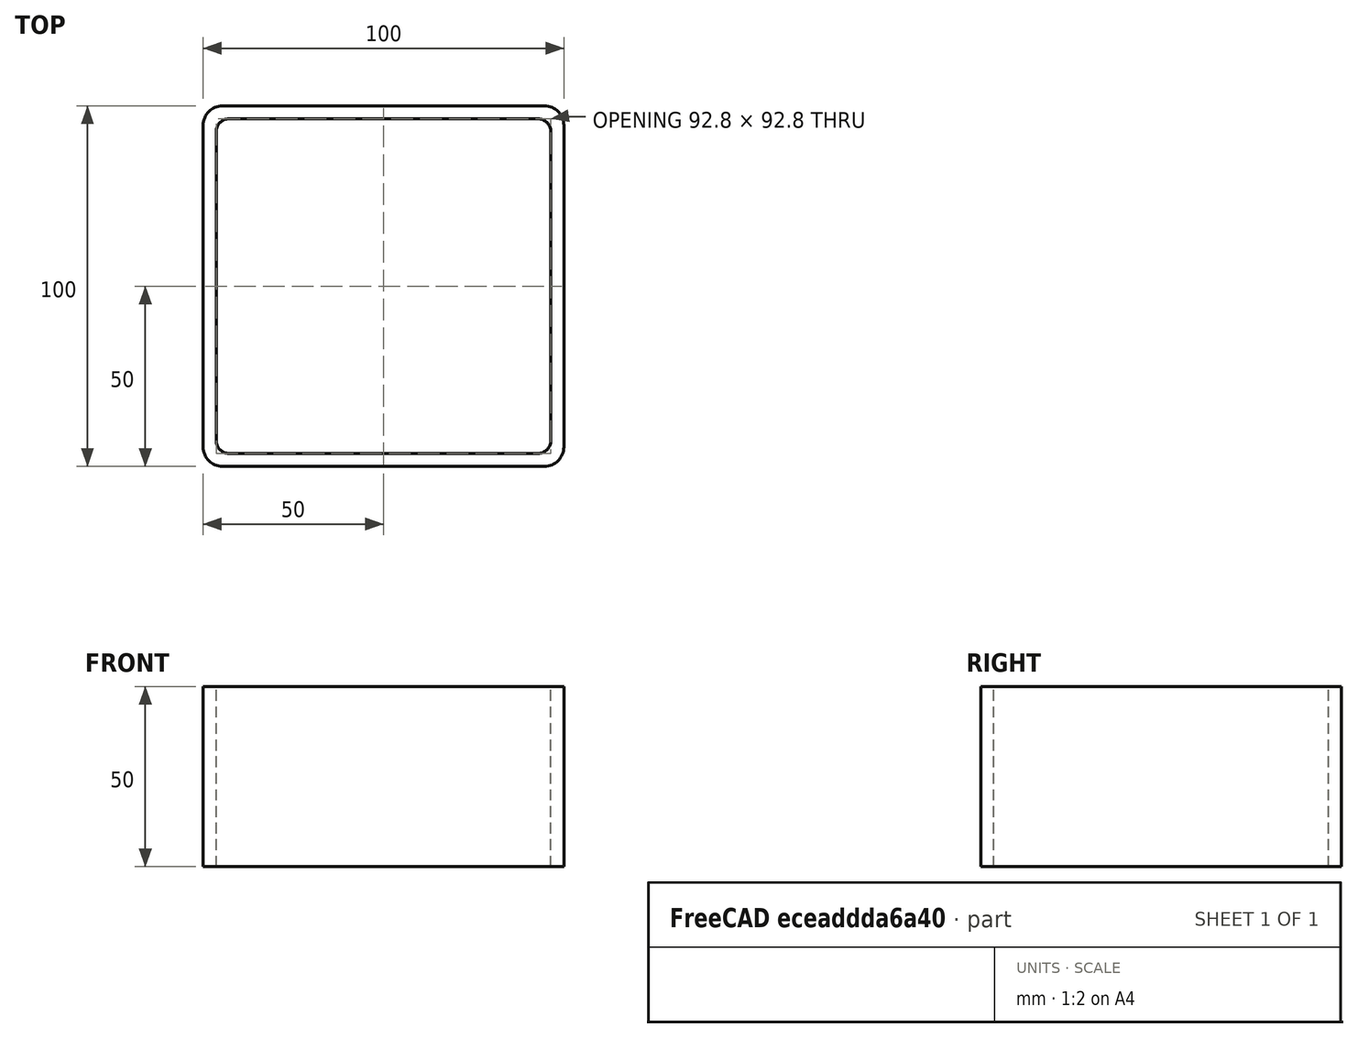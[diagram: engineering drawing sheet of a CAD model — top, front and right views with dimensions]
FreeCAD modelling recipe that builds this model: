
FCSTD DOCUMENT  (FreeCAD 0.15R4671 (Git))
Label: Square hollow section 100x100x3.6 EN10219 S235JRH
License: All rights reserved
LicenseURL: http://en.wikipedia.org/wiki/All_rights_reserved
objects: Sketcher::SketchObject×1, Part::Extrusion×1
note: 2 computed .brp shape members not serialized (recipe doc carries the construction recipe); baked Part::Feature solids carry a one-line shape summary decoded from their .brp

FEATURE [Sketcher::SketchObject] Sketch
  sketch-geometry (16):
    g0: LineSegment StartX=-42.8 StartY=46.4 StartZ=0 EndX=42.8 EndY=46.4 EndZ=0
    g1: LineSegment StartX=46.4 StartY=42.8 StartZ=0 EndX=46.4 EndY=-42.8 EndZ=0
    g2: LineSegment StartX=42.8 StartY=-46.4 StartZ=0 EndX=-42.8 EndY=-46.4 EndZ=0
    g3: LineSegment StartX=-46.4 StartY=-42.8 StartZ=0 EndX=-46.4 EndY=42.8 EndZ=0
    g4: LineSegment StartX=-44.6 StartY=50 StartZ=0 EndX=44.6 EndY=50 EndZ=0
    g5: LineSegment StartX=50 StartY=44.6 StartZ=0 EndX=50 EndY=-44.6 EndZ=0
    g6: LineSegment StartX=44.6 StartY=-50 StartZ=0 EndX=-44.6 EndY=-50 EndZ=0
    g7: LineSegment StartX=-50 StartY=-44.6 StartZ=0 EndX=-50 EndY=44.6 EndZ=0
    g8: ArcOfCircle CenterX=-42.8 CenterY=42.8 CenterZ=0 NormalX=0 NormalY=0 NormalZ=1 Radius=3.6 StartAngle=1.5708 EndAngle=3.14159
    g9: ArcOfCircle CenterX=42.8 CenterY=42.8 CenterZ=0 NormalX=0 NormalY=0 NormalZ=1 Radius=3.6 StartAngle=0 EndAngle=1.5708
    g10: ArcOfCircle CenterX=42.8 CenterY=-42.8 CenterZ=0 NormalX=0 NormalY=0 NormalZ=1 Radius=3.6 StartAngle=4.71239 EndAngle=6.28319
    g11: ArcOfCircle CenterX=-42.8 CenterY=-42.8 CenterZ=0 NormalX=0 NormalY=0 NormalZ=1 Radius=3.6 StartAngle=3.14159 EndAngle=4.71239
    g12: ArcOfCircle CenterX=44.6 CenterY=44.6 CenterZ=0 NormalX=0 NormalY=0 NormalZ=1 Radius=5.4 StartAngle=0 EndAngle=1.5708
    g13: ArcOfCircle CenterX=44.6 CenterY=-44.6 CenterZ=0 NormalX=0 NormalY=0 NormalZ=1 Radius=5.4 StartAngle=4.71239 EndAngle=6.28319
    g14: ArcOfCircle CenterX=-44.6 CenterY=-44.6 CenterZ=0 NormalX=0 NormalY=0 NormalZ=1 Radius=5.4 StartAngle=3.14159 EndAngle=4.71239
    g15: ArcOfCircle CenterX=-44.6 CenterY=44.6 CenterZ=0 NormalX=0 NormalY=0 NormalZ=1 Radius=5.4 StartAngle=1.5708 EndAngle=3.14159
  constraints (36):
    c: Horizontal(g2)
    c: Vertical(g3)
    c: Horizontal(g6)
    c: Vertical(g7)
    c: Tangent(g3,g8) = 1.5708
    c: Tangent(g0,g8) = 1.5708
    c: Tangent(g0,g9) = 1.5708
    c: Tangent(g1,g9) = 1.5708
    c: Tangent(g1,g10) = 1.5708
    c: Tangent(g2,g10) = 1.5708
    c: Tangent(g2,g11) = 1.5708
    c: Tangent(g3,g11) = 1.5708
    c: Tangent(g4,g12) = 1.5708
    c: Tangent(g5,g12) = 1.5708
    c: Tangent(g5,g13) = 1.5708
    c: Tangent(g6,g13) = 1.5708
    c: Tangent(g6,g14) = 1.5708
    c: Tangent(g7,g14) = 1.5708
    c: Tangent(g7,g15) = 1.5708
    c: Tangent(g4,g15) = 1.5708
    c: Equal(g9,g8)
    c: Equal(g9,g11)
    c: Equal(g9,g10)
    c: Equal(g12,g15)
    c: Equal(g12,g14)
    c: Equal(g12,g13)
    c: Symmetric(g4,g6,g-1)
    c: Symmetric(g7,g5,g-2)
    c: DistanceY(g4,g6) = -100
    c: DistanceX(g7,g5) = 100
    c: Symmetric(g3,g1,g-2)
    c: Symmetric(g0,g2,g-1)
    c: DistanceY(g0,g4) = 3.6
    c: DistanceX(g5,g1) = -3.6
    c: Radius(g9) = 3.6
    c: Radius(g12) = 5.4
FEATURE [Part::Extrusion] Extrude  label="Square hollow section 100x100x3.6 EN10219 S235JRH"
  Base = -> Sketch
  Dir = (0,0,50)
  Solid = true
